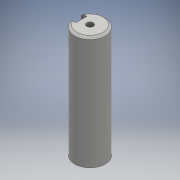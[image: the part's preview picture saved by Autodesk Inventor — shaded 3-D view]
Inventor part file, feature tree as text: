
AUTODESK INVENTOR PART (.ipt)
format: ipt  version: 2016 (Build 200138000, 138)  size: 116,736 bytes
history: native  units: mm
features: extrude x2, sketch x2, hole x1, plane x1, chamfer x1, projected_geometry x1
ambient origin geometry x8: Origin, YZ Plane, XZ Plane, XY Plane, X Axis, Y Axis, Z Axis, Center Point
bodies: Solid1 (feature_tree)
feature tree (8):
  extrude  "Extrusion1"  Depth=52.0mm TaperAngle=0.0deg
  hole  "Hole1"  [1 undecoded]
  plane  "Work Plane1"
  extrude  "Extrusion2"  TaperAngle=0.0deg  [1 undecoded]
  chamfer  "Chamfer1"  Distance=3.0mm
  sketch  "Sketch1"  dims[d0=14.0mm d1=52.0mm d2=0.0mm]
  sketch  "Sketch2"  dims[d3=10.0mm d4=10.0mm d5=3.0mm d6=6.0mm d7=4.0mm d8=2.0mm d9=90.0deg d10=13.0mm d11=0.0mm d12=5.0mm d14=0.0mm d17=3.0mm d18=0.0mm d19=1.0mm d20=2.0mm d21=45.0deg]
  projected_geometry  "Projected Loop1"
note: 2 required parameter values undecoded (feature->parameter linkage not recoverable at this tier; creation-order binding heuristic only, values carry confidence <= 0.55)
